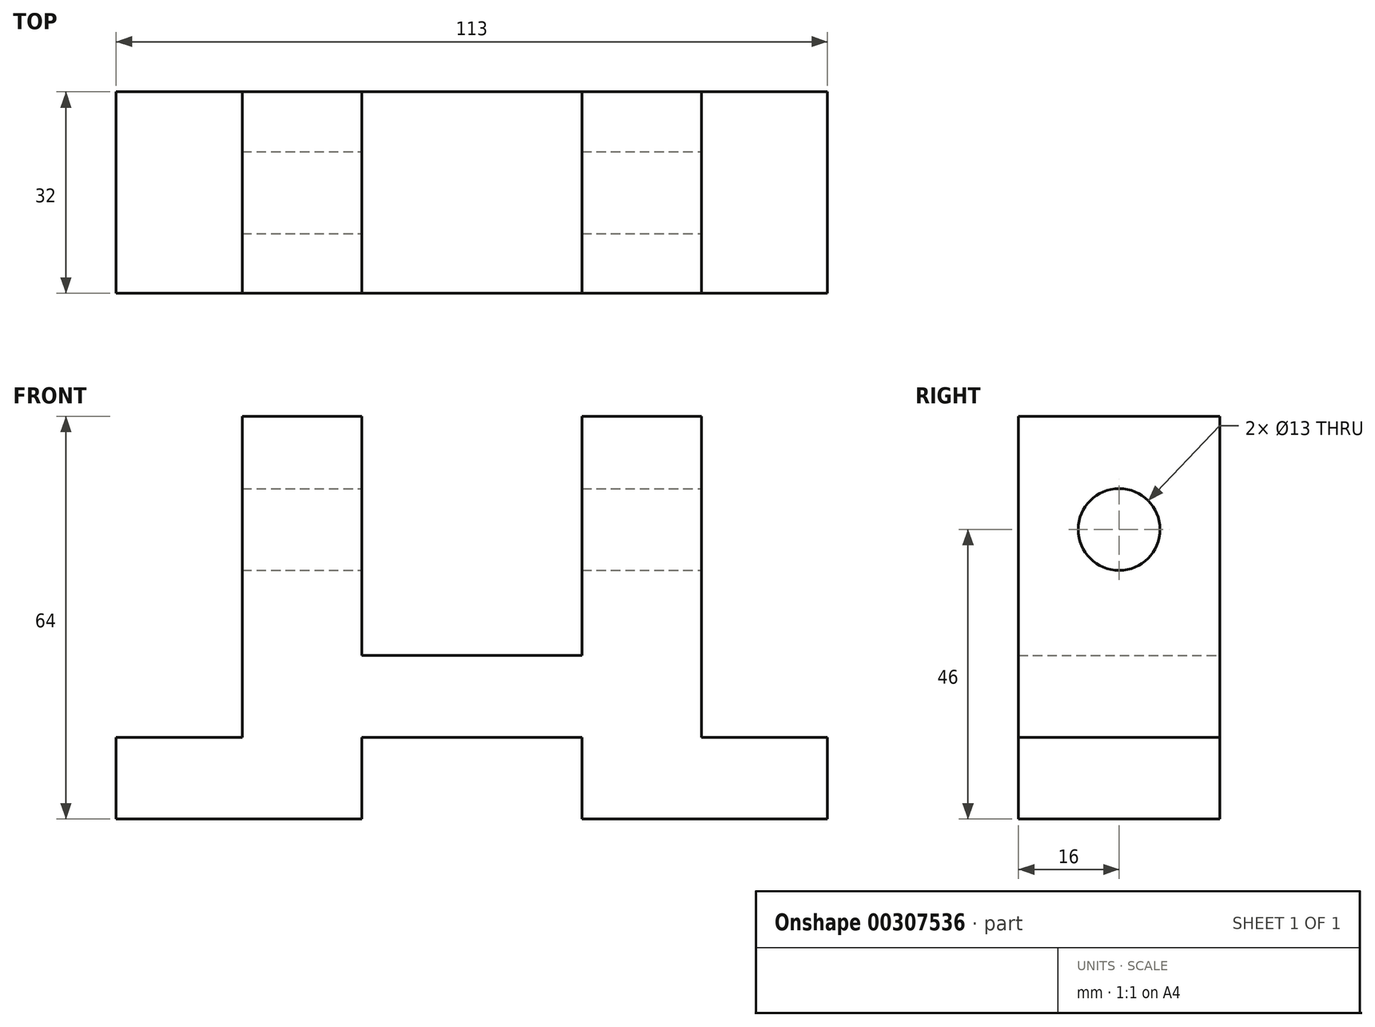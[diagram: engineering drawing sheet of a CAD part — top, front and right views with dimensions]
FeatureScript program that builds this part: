
annotation { "Feature Type Name" : "Feature", "Feature Type Description" : "" }
export const myFeature = defineFeature(function(context is Context, id is Id, definition is map)
    precondition{}
    {
        {
            var Q0;
            Q0=qCreatedBy(makeId("Front.planeOp"),FACE);
            var sketch = newSketch(context, id + "F0", { "sketchPlane" : qUnion([Q0])});
            skLineSegment(sketch, "E0.bottom", {"start": v(0, 0) * mm, "end": v(39, 0) * mm});
            skLineSegment(sketch, "E0.top", {"start": v(20, 64) * mm, "end": v(39, 64) * mm});
            skLineSegment(sketch, "E0.left", {"start": v(0, 0) * mm, "end": v(0, 13) * mm});
            skLineSegment(sketch, "E0.right", {"start": v(113, 0) * mm, "end": v(113, 13) * mm});
            skLineSegment(sketch, "E1", {"start": v(39, 0) * mm, "end": v(39, 13) * mm});
            skLineSegment(sketch, "E2", {"start": v(39, 13) * mm, "end": v(74, 13) * mm});
            skLineSegment(sketch, "E3", {"start": v(74, 13) * mm, "end": v(74, 0) * mm});
            skLineSegment(sketch, "E4", {"start": v(74, 0) * mm, "end": v(113, 0) * mm});
            skLineSegment(sketch, "E5", {"start": v(113, 13) * mm, "end": v(93, 13) * mm});
            skLineSegment(sketch, "E6", {"start": v(93, 13) * mm, "end": v(93, 64) * mm});
            skLineSegment(sketch, "E7", {"start": v(93, 64) * mm, "end": v(74, 64) * mm});
            skLineSegment(sketch, "E8", {"start": v(74, 64) * mm, "end": v(74, 26) * mm});
            skLineSegment(sketch, "E9", {"start": v(74, 26) * mm, "end": v(39, 26) * mm});
            skLineSegment(sketch, "E10", {"start": v(39, 26) * mm, "end": v(39, 64) * mm});
            skLineSegment(sketch, "E11", {"start": v(39, 64) * mm, "end": v(20, 64) * mm});
            skLineSegment(sketch, "E12", {"start": v(20, 64) * mm, "end": v(20, 13) * mm});
            skLineSegment(sketch, "E13", {"start": v(20, 13) * mm, "end": v(0, 13) * mm});
            skLineSegment(sketch, "E14", {"start": v(0, 13) * mm, "end": v(0, 0) * mm});
            skLineSegment(sketch, "E15.trimOffspring", {"start": v(74, 64) * mm, "end": v(93, 64) * mm});
            skSolve(sketch);
        }
        {
            var Q0;
            Q0 = qSketchRegion(id + "F0", true);
            extrude(context, id + "F1", {"entities" : qUnion([Q0]), "endBound" : BoundingType.SYMMETRIC, "depth" : 32 * mm});
        }
        {
            var Q0;
            Q0=makeQuery(id+"F1.opExtrude","SWEPT_FACE",FACE,{"disambiguationData":[OSD([sQuery(id+"F0.wireOp",EDGE,"E6")])]});
            var sketch = newSketch(context, id + "F2", { "sketchPlane" : qUnion([Q0])});
            skCircle(sketch, "E16", {"center": v(0, 46) * mm, "radius": 6.5 * mm});
            skPoint(sketch, "E17.start.orphan", {"position": v(0, 64) * mm});
            skSolve(sketch);
        }
        {
            var Q0;
            Q0 = qSketchRegion(id + "F2", true);
            extrude(context, id + "F3", {"entities" : qUnion([Q0]), "operationType" : NewBodyOperationType.REMOVE, "endBound" : BoundingType.THROUGH_ALL, "oppositeDirection" : true, "depth" : 25 * mm});
        }
        {
            var Q0;
            Q0 = qSketchRegion(id + "F2", true);
            extrude(context, id + "F4", {"entities" : qUnion([Q0]), "operationType" : NewBodyOperationType.REMOVE, "endBound" : BoundingType.THROUGH_ALL, "oppositeDirection" : true, "depth" : 25 * mm});
        }
    });
